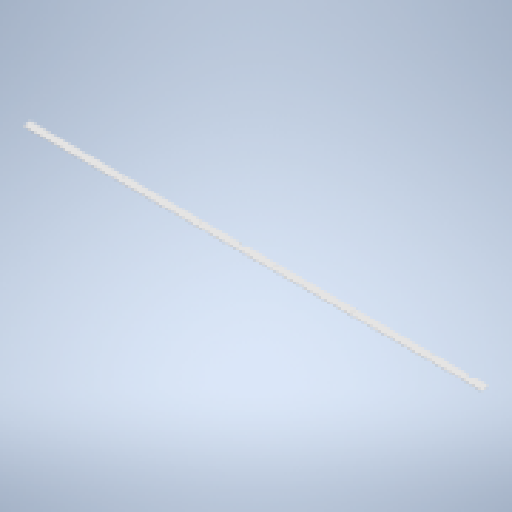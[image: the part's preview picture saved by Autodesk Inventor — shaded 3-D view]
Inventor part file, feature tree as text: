
AUTODESK INVENTOR PART (.ipt)
format: ipt  version: 2025 (Build 290162010, 162A)  size: 342,528 bytes
history: native  units: mm
features: sketch x4, other x3, extrude x2, sheet_metal_op x1, pattern_linear x1, projected_geometry x1
ambient origin geometry x8: Origin, YZ Plane, XZ Plane, XY Plane, X Axis, Y Axis, Z Axis, Center Point
bodies: Body1 (feature_tree)
feature tree (12):
  sheet_metal_op  "Face3"
  extrude  "Extrusion3"  Depth=2980.0mm
  pattern_linear  "Rectangular Pattern2"  Spacing1=26.0mm  [1 undecoded]
  extrude  "Extrusion4"  TaperAngle=0.0deg  [1 undecoded]
  other  "Mark1"
  sketch  "Sketch8"  dims[d37=50.0mm d38=2980.0mm]
  other  "Plate5"
  sketch  "Sketch9"  dims[d39=3.0mm]
  sketch  "Sketch10"  dims[d40=116.0mm]
  projected_geometry  "Projected Loop2"
  sketch  "Sketch11"  dims[d41=3.2mm d42=26.0mm d43=0.0mm d44=0.0mm d45=60.0mm d47=500.0mm d48=40.0mm d49=40.0mm d50=1480.0mm d51=125.0mm d52=0.0mm d53=0.0mm d54=200.0mm d55=15.0mm]
  other  "Definition1"
note: 2 required parameter values undecoded (feature->parameter linkage not recoverable at this tier; creation-order binding heuristic only, values carry confidence <= 0.55)
